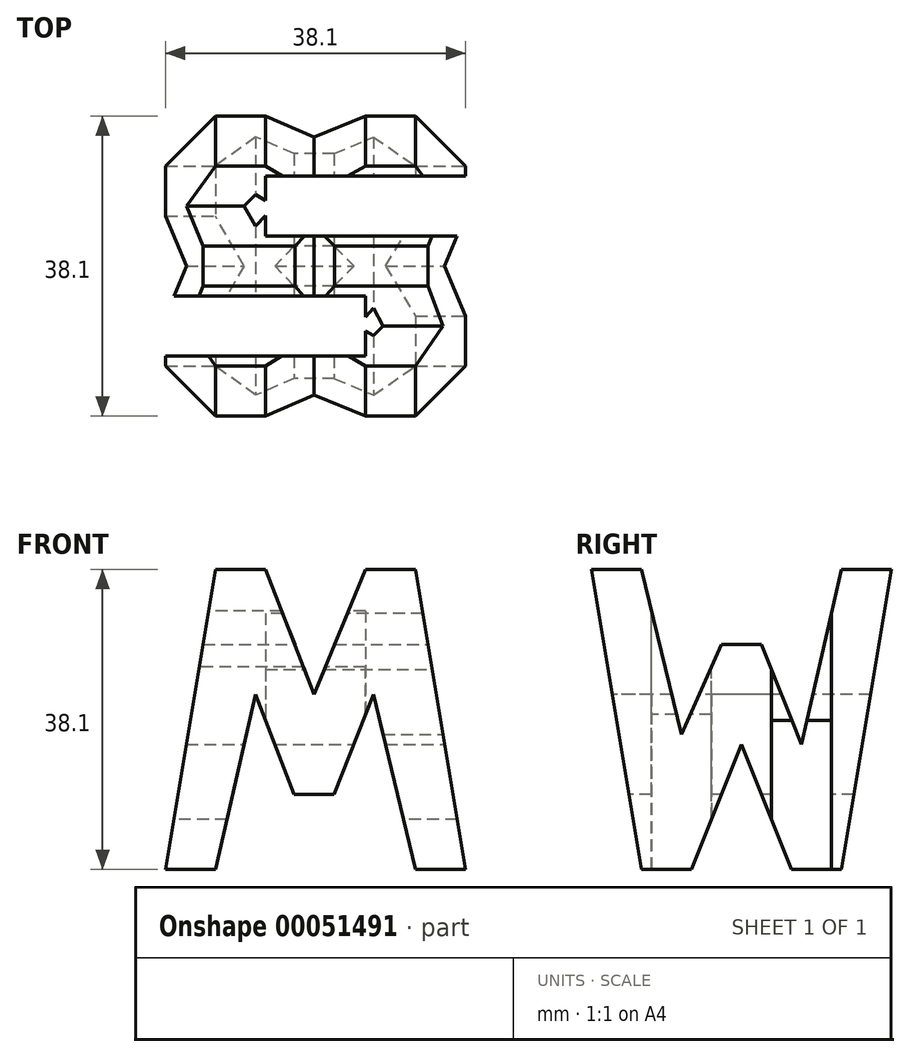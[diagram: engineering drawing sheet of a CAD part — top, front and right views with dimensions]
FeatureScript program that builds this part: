
annotation { "Feature Type Name" : "Feature", "Feature Type Description" : "" }
export const myFeature = defineFeature(function(context is Context, id is Id, definition is map)
    precondition{}
    {
        {
            var Q0;
            Q0=qCreatedBy(makeId("Front.planeOp"),FACE);
            var sketch = newSketch(context, id + "F0", { "sketchPlane" : qUnion([Q0])});
            skLineSegment(sketch, "E0", {"start": v(0, 0) * mm, "end": v(0, 38.1) * mm});
            skLineSegment(sketch, "E1", {"start": v(0, 38.1) * mm, "end": v(38.1, 38.1) * mm});
            skLineSegment(sketch, "E2", {"start": v(38.1, 38.1) * mm, "end": v(38.1, 0) * mm});
            skLineSegment(sketch, "E3", {"start": v(38.1, 0) * mm, "end": v(0, 0) * mm});
            skSolve(sketch);
        }
        {
            var Q0;
            Q0 = qSketchRegion(id + "F0", true);
            extrude(context, id + "F1", {"entities" : qUnion([Q0]), "depth" : 38.1 * mm});
        }
        {
            var Q0;
            Q0=qCreatedBy(makeId("Front.planeOp"),FACE);
            cPlane(context, id + "F2", {"entities" : qUnion([Q0]), "cplaneType" : CPlaneType.OFFSET, "offset" : 38.1 * mm, "width" : 152.4 * mm, "height" : 152.4 * mm});
        }
        {
            var Q0;
            Q0=qCreatedBy(makeId("Top.planeOp"),FACE);
            cPlane(context, id + "F3", {"entities" : qUnion([Q0]), "cplaneType" : CPlaneType.OFFSET, "offset" : 38.1 * mm, "width" : 152.4 * mm, "height" : 152.4 * mm});
        }
        {
            var Q0;
            Q0=makeQuery(id+"F1.opExtrude","SWEPT_FACE",FACE,{"disambiguationData":[OSD([sQuery(id+"F0.wireOp",EDGE,"E2")])]});
            var sketch = newSketch(context, id + "F4", { "sketchPlane" : qUnion([Q0])});
            skLineSegment(sketch, "E4", {"start": v(-31.75, 0) * mm, "end": v(-25.4, 0) * mm});
            skLineSegment(sketch, "E5", {"start": v(-12.7, 0) * mm, "end": v(-6.35, 0) * mm});
            skLineSegment(sketch, "E6", {"start": v(-31.75, 0) * mm, "end": v(-38.1, 38.1) * mm});
            skLineSegment(sketch, "E7", {"start": v(-6.35, 0) * mm, "end": v(0, 38.1) * mm});
            skLineSegment(sketch, "E8", {"start": v(-25.4, 0) * mm, "end": v(-19.05, 15.87) * mm});
            skLineSegment(sketch, "E9", {"start": v(-12.7, 0) * mm, "end": v(-19.05, 15.88) * mm});
            skLineSegment(sketch, "E10", {"start": v(-16.5, 28.57) * mm, "end": v(-21.59, 28.57) * mm});
            skLineSegment(sketch, "E11", {"start": v(-38.1, 38.1) * mm, "end": v(-31.75, 38.1) * mm});
            skLineSegment(sketch, "E12", {"start": v(-31.75, 38.1) * mm, "end": v(-26.67, 17.14) * mm});
            skLineSegment(sketch, "E13", {"start": v(-26.67, 17.14) * mm, "end": v(-21.59, 28.57) * mm});
            skLineSegment(sketch, "E14", {"start": v(-16.5, 28.57) * mm, "end": v(-11.43, 15.87) * mm});
            skLineSegment(sketch, "E15", {"start": v(-6.35, 38.1) * mm, "end": v(-11.43, 15.87) * mm});
            skLineSegment(sketch, "E16", {"start": v(-6.35, 38.1) * mm, "end": v(0, 38.1) * mm});
            skLineSegment(sketch, "E17", {"start": v(-6.35, 38.1) * mm, "end": v(-11.43, 38.1) * mm});
            skLineSegment(sketch, "E18.bottom", {"start": v(0, 0) * mm, "end": v(-38.1, 0) * mm});
            skLineSegment(sketch, "E18.top", {"start": v(0, 38.1) * mm, "end": v(-38.1, 38.1) * mm});
            skLineSegment(sketch, "E18.left", {"start": v(0, 0) * mm, "end": v(0, 38.1) * mm});
            skLineSegment(sketch, "E18.right", {"start": v(-38.1, 0) * mm, "end": v(-38.1, 38.1) * mm});
            skSolve(sketch);
        }
        {
            var Q0;
            Q0=makeQuery(id+"F4.imprint","IMPRINT",FACE,{"disambiguationData":[TD([[makeQuery(id+"F4.imprint","IMPRINT",EDGE,{"derivedFrom":sQuery(id+"F4.wireOp",EDGE,"E10")}),-1.0]])]});
            var Q1;
            {var subQ0=sQuery(id+"F4.wireOp",EDGE,"E6");Q1=makeQuery(id+"F4.imprint","IMPRINT",FACE,{"disambiguationData":[TD([[makeQuery(id+"F4.imprint","IMPRINT",EDGE,{"derivedFrom":subQ0}),1.0]])]});}
            var Q2;
            {var subQ0=sQuery(id+"F4.wireOp",EDGE,"E8");Q2=makeQuery(id+"F4.imprint","IMPRINT",FACE,{"disambiguationData":[TD([[makeQuery(id+"F4.imprint","IMPRINT",EDGE,{"derivedFrom":subQ0}),-1.0]])]});}
            var Q3;
            {var subQ0=sQuery(id+"F4.wireOp",EDGE,"E7");Q3=makeQuery(id+"F4.imprint","IMPRINT",FACE,{"disambiguationData":[TD([[makeQuery(id+"F4.imprint","IMPRINT",EDGE,{"derivedFrom":subQ0}),-1.0]])]});}
            extrude(context, id + "F5", {"entities" : qUnion([Q0, Q1, Q2, Q3]), "operationType" : NewBodyOperationType.REMOVE, "oppositeDirection" : true, "depth" : 50.8 * mm});
        }
        {
            var Q0;
            Q0=qCreatedBy(id+"F2.planeOp",FACE);
            var sketch = newSketch(context, id + "F6", { "sketchPlane" : qUnion([Q0])});
            skLineSegment(sketch, "E19", {"start": v(0, 0) * mm, "end": v(6.35, 0) * mm});
            skLineSegment(sketch, "E20", {"start": v(6.35, 0) * mm, "end": v(11.43, 0) * mm});
            skLineSegment(sketch, "E21", {"start": v(0, 38.13) * mm, "end": v(6.35, 38.13) * mm});
            skLineSegment(sketch, "E22", {"start": v(6.35, 38.13) * mm, "end": v(0, 0) * mm});
            skLineSegment(sketch, "E23", {"start": v(6.35, 0) * mm, "end": v(11.43, 22.23) * mm});
            skLineSegment(sketch, "E24", {"start": v(6.35, 38.13) * mm, "end": v(12.7, 38.13) * mm});
            skLineSegment(sketch, "E25", {"start": v(12.7, 38.13) * mm, "end": v(18.88, 38.13) * mm});
            skLineSegment(sketch, "E26", {"start": v(18.88, 38.13) * mm, "end": v(25.4, 38.13) * mm});
            skLineSegment(sketch, "E27", {"start": v(25.4, 38.13) * mm, "end": v(31.75, 38.13) * mm});
            skLineSegment(sketch, "E28.bottom", {"start": v(0, 0) * mm, "end": v(38.1, 0) * mm});
            skLineSegment(sketch, "E28.top", {"start": v(0, 38.1) * mm, "end": v(38.1, 38.1) * mm});
            skLineSegment(sketch, "E28.left", {"start": v(0, 0) * mm, "end": v(0, 38.1) * mm});
            skLineSegment(sketch, "E28.right", {"start": v(38.1, 0) * mm, "end": v(38.1, 38.1) * mm});
            skLineSegment(sketch, "E29", {"start": v(31.75, 38.13) * mm, "end": v(38.1, 38.1) * mm});
            skLineSegment(sketch, "E30", {"start": v(18.88, 38.13) * mm, "end": v(18.88, 22.26) * mm});
            skLineSegment(sketch, "E31", {"start": v(12.7, 38.13) * mm, "end": v(18.88, 22.26) * mm});
            skLineSegment(sketch, "E32", {"start": v(25.4, 38.13) * mm, "end": v(18.88, 22.26) * mm});
            skLineSegment(sketch, "E33", {"start": v(38.1, 0) * mm, "end": v(31.75, 0) * mm});
            skLineSegment(sketch, "E34", {"start": v(31.75, 0) * mm, "end": v(26.67, 0) * mm});
            skLineSegment(sketch, "E35", {"start": v(31.75, 38.13) * mm, "end": v(38.1, 0) * mm});
            skLineSegment(sketch, "E36", {"start": v(31.75, 0) * mm, "end": v(26.4, 22.23) * mm});
            skLineSegment(sketch, "E37", {"start": v(18.88, 22.26) * mm, "end": v(18.88, 9.56) * mm});
            skLineSegment(sketch, "E38", {"start": v(18.88, 9.56) * mm, "end": v(21.42, 9.56) * mm});
            skLineSegment(sketch, "E39", {"start": v(18.88, 9.56) * mm, "end": v(16.34, 9.56) * mm});
            skLineSegment(sketch, "E40", {"start": v(11.43, 22.23) * mm, "end": v(16.34, 9.56) * mm});
            skLineSegment(sketch, "E41", {"start": v(26.4, 22.23) * mm, "end": v(21.42, 9.56) * mm});
            skSolve(sketch);
        }
        {
            var Q0;
            {var subQ2=sQuery(id+"F6.wireOp",EDGE,"E23");Q0=makeQuery(id+"F6.imprint","IMPRINT",FACE,{"disambiguationData":[TD([[makeQuery(id+"F6.imprint","IMPRINT",EDGE,{"derivedFrom":subQ2}),-1.0]])]});}
            var Q1;
            {var subQ0=sQuery(id+"F6.wireOp",EDGE,"E31");var subQ1=sQuery(id+"F6.wireOp",EDGE,"E28.top");var subQ2=makeQuery(id+"F6.imprint","INTERSECT",VERTEX,{"derivedFrom":[subQ1,subQ0]});Q1=makeQuery(id+"F6.imprint","IMPRINT",FACE,{"disambiguationData":[TD([[makeQuery(id+"F6.imprint","IMPRINT",EDGE,{"disambiguationData":[TD([[subQ2,-1.0]])],"derivedFrom":subQ1}),-1.0]])]});}
            var Q2;
            {var subQ0=sQuery(id+"F6.wireOp",EDGE,"E30");var subQ1=sQuery(id+"F6.wireOp",EDGE,"E28.top");var subQ2=makeQuery(id+"F6.imprint","INTERSECT",VERTEX,{"derivedFrom":[subQ1,subQ0]});Q2=makeQuery(id+"F6.imprint","IMPRINT",FACE,{"disambiguationData":[TD([[makeQuery(id+"F6.imprint","IMPRINT",EDGE,{"disambiguationData":[TD([[subQ2,-1.0]])],"derivedFrom":subQ1}),-1.0]])]});}
            var Q3;
            {var subQ0=sQuery(id+"F6.wireOp",EDGE,"E28.right");Q3=makeQuery(id+"F6.imprint","IMPRINT",FACE,{"disambiguationData":[TD([[makeQuery(id+"F6.imprint","IMPRINT",EDGE,{"derivedFrom":subQ0}),1.0]])]});}
            var Q4;
            {var subQ0=sQuery(id+"F6.wireOp",EDGE,"E28.left");Q4=makeQuery(id+"F6.imprint","IMPRINT",FACE,{"disambiguationData":[TD([[makeQuery(id+"F6.imprint","IMPRINT",EDGE,{"derivedFrom":subQ0}),-1.0]])]});}
            extrude(context, id + "F7", {"entities" : qUnion([Q0, Q1, Q2, Q3, Q4]), "operationType" : NewBodyOperationType.REMOVE, "oppositeDirection" : true, "depth" : 127 * mm});
        }
        {
            var Q0;
            Q0=qCreatedBy(id+"F3.planeOp",FACE);
            var sketch = newSketch(context, id + "F8", { "sketchPlane" : qUnion([Q0])});
            skLineSegment(sketch, "E42", {"start": v(0, 0) * mm, "end": v(0, -7.62) * mm});
            skLineSegment(sketch, "E43", {"start": v(0, -7.62) * mm, "end": v(0, -15.24) * mm});
            skLineSegment(sketch, "E44", {"start": v(0, -15.24) * mm, "end": v(0, -22.86) * mm});
            skLineSegment(sketch, "E45", {"start": v(0, -22.86) * mm, "end": v(0, -30.48) * mm});
            skLineSegment(sketch, "E46", {"start": v(0, -30.48) * mm, "end": v(0, -38.1) * mm});
            skLineSegment(sketch, "E47", {"start": v(0, -38.1) * mm, "end": v(12.7, -38.1) * mm});
            skLineSegment(sketch, "E48", {"start": v(12.7, -38.1) * mm, "end": v(25.4, -38.1) * mm});
            skLineSegment(sketch, "E49", {"start": v(25.4, -38.1) * mm, "end": v(38.1, -38.1) * mm});
            skLineSegment(sketch, "E50", {"start": v(0, -30.48) * mm, "end": v(12.7, -30.48) * mm});
            skLineSegment(sketch, "E51", {"start": v(0, -22.86) * mm, "end": v(12.7, -22.86) * mm});
            skLineSegment(sketch, "E52", {"start": v(12.7, -22.86) * mm, "end": v(25.4, -22.86) * mm});
            skLineSegment(sketch, "E53", {"start": v(12.7, -30.48) * mm, "end": v(25.4, -30.48) * mm});
            skLineSegment(sketch, "E54", {"start": v(25.4, -22.86) * mm, "end": v(25.4, -30.48) * mm});
            skSolve(sketch);
        }
        {
            var Q0;
            Q0=makeQuery(id+"F8.imprint","IMPRINT",FACE,{"disambiguationData":[TD([[makeQuery(id+"F8.imprint","IMPRINT",EDGE,{"derivedFrom":sQuery(id+"F8.wireOp",EDGE,"E45")}),1.0]])]});
            extrude(context, id + "F9", {"entities" : qUnion([Q0]), "operationType" : NewBodyOperationType.REMOVE, "oppositeDirection" : true, "depth" : 50.8 * mm});
        }
        {
            var Q0;
            Q0=qCreatedBy(id+"F3.planeOp",FACE);
            var sketch = newSketch(context, id + "F10", { "sketchPlane" : qUnion([Q0])});
            skLineSegment(sketch, "E55", {"start": v(0, 0) * mm, "end": v(0, -7.62) * mm});
            skLineSegment(sketch, "E56", {"start": v(0, -7.62) * mm, "end": v(0, -15.24) * mm});
            skLineSegment(sketch, "E57", {"start": v(0, -15.24) * mm, "end": v(0, -38.1) * mm});
            skLineSegment(sketch, "E58", {"start": v(0, -38.1) * mm, "end": v(12.7, -38.1) * mm});
            skLineSegment(sketch, "E59", {"start": v(12.7, -38.1) * mm, "end": v(38.1, -38.1) * mm});
            skLineSegment(sketch, "E60", {"start": v(38.1, -38.1) * mm, "end": v(38.1, -15.24) * mm});
            skLineSegment(sketch, "E61", {"start": v(38.1, -15.24) * mm, "end": v(38.1, -7.62) * mm});
            skLineSegment(sketch, "E62", {"start": v(38.1, -15.24) * mm, "end": v(12.7, -15.24) * mm});
            skLineSegment(sketch, "E63", {"start": v(38.1, -7.62) * mm, "end": v(12.7, -7.62) * mm});
            skLineSegment(sketch, "E64", {"start": v(12.7, -7.62) * mm, "end": v(12.7, -15.24) * mm});
            skSolve(sketch);
        }
        {
            var Q0;
            Q0=makeQuery(id+"F10.imprint","IMPRINT",FACE,{"disambiguationData":[TD([[makeQuery(id+"F10.imprint","IMPRINT",EDGE,{"derivedFrom":sQuery(id+"F10.wireOp",EDGE,"E61")}),1.0]])]});
            extrude(context, id + "F11", {"entities" : qUnion([Q0]), "operationType" : NewBodyOperationType.REMOVE, "oppositeDirection" : true, "depth" : 50.8 * mm});
        }
    });
